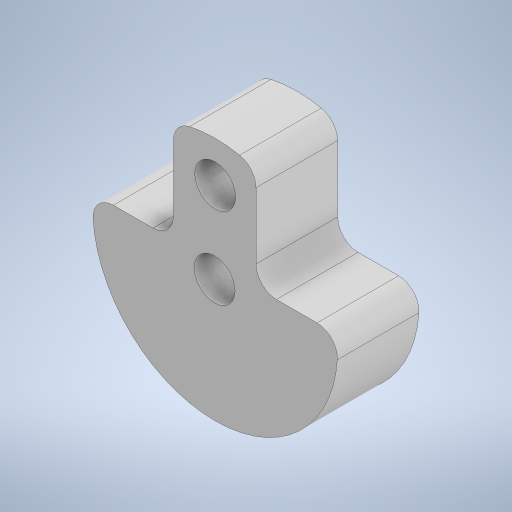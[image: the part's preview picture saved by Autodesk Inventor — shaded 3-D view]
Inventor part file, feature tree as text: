
AUTODESK INVENTOR PART (.ipt)
format: ipt  version: 2023 (Build 270158000, 158)  size: 253,952 bytes
history: native  units: in
note: dims shown in document units (in); Inventor stores cm internally (conversion verified against a paired STEP export)
features: extrude x1, sketch x1
ambient origin geometry x8: Origin, YZ Plane, XZ Plane, XY Plane, X Axis, Y Axis, Z Axis, Center Point
bodies: Solid1 (feature_tree)
feature tree (2):
  extrude  "Extrusion1"  Depth=0.5in
  sketch  "Sketch1"  dims[d2=1.5in d3=0.25in d6=0.25in d7=0.5in d8=0.0in d11=0.625in d12=0.125in d10=0.5in d13=0.0344in]
